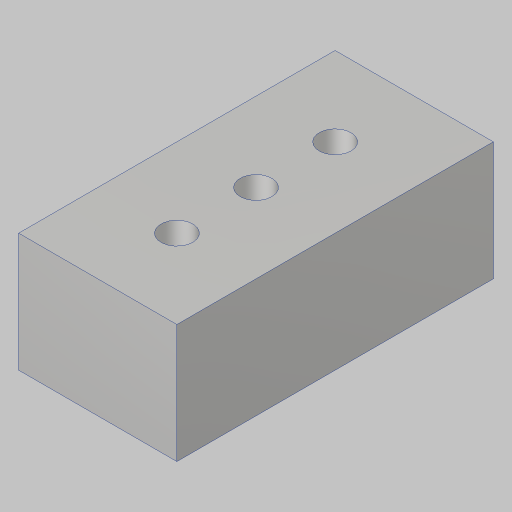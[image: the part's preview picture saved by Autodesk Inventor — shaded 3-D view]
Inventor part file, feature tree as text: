
AUTODESK INVENTOR PART (.ipt)
format: ipt  version: 2023.5 (Build 275446000, 446)  size: 99,328 bytes
history: native  units: in
note: dims shown in document units (in); Inventor stores cm internally (conversion verified against a paired STEP export)
features: sketch x2, extrude x1, hole x1
ambient origin geometry x8: Origin, YZ Plane, XZ Plane, XY Plane, X Axis, Y Axis, Z Axis, Center Point
bodies: Solid1 (feature_tree)
feature tree (4):
  extrude  "Extrusion1"  Depth=2.0in
  hole  "Hole1"  [1 undecoded]
  sketch  "Sketch2"  dims[d0=1.0in d1=2.0in]
  sketch  "Sketch3"  dims[d2=0.75in d3=0.0in d4=0.5in d5=0.5in d6=0.201in d7=0.75in d8=0.385in d9=0.25in d10=0.5635in d11=1.0in d12=0.8108in]
note: 1 required parameter value undecoded (feature->parameter linkage not recoverable at this tier; creation-order binding heuristic only, values carry confidence <= 0.55)
